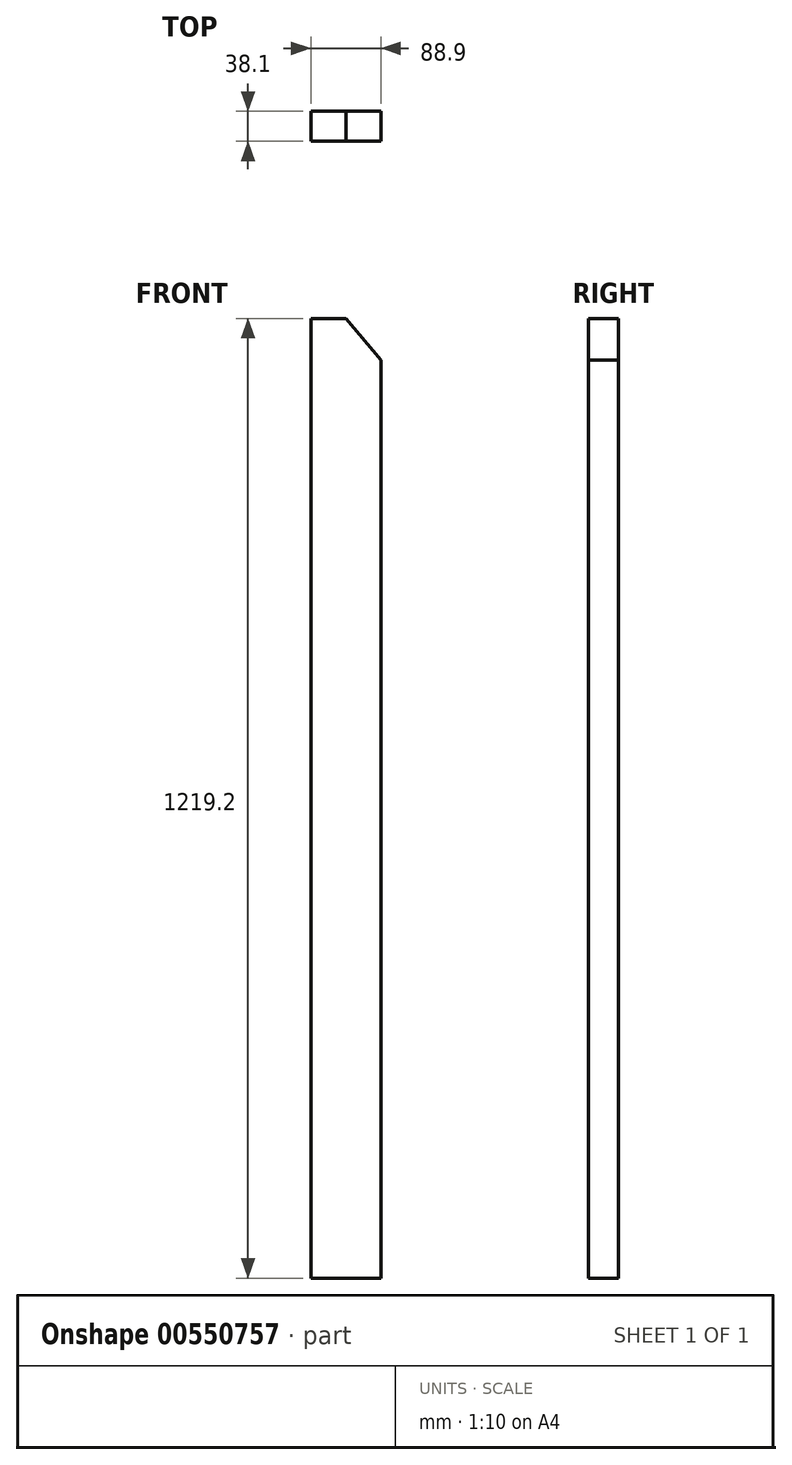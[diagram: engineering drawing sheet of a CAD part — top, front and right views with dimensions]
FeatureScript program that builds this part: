
annotation { "Feature Type Name" : "Feature", "Feature Type Description" : "" }
export const myFeature = defineFeature(function(context is Context, id is Id, definition is map)
    precondition{}
    {
        {
            var Q0;
            Q0=qCreatedBy(makeId("Front.planeOp"),FACE);
            var sketch = newSketch(context, id + "F0", { "sketchPlane" : qUnion([Q0])});
            skLineSegment(sketch, "E0", {"start": v(0, 0) * mm, "end": v(88.9, 0) * mm});
            skLineSegment(sketch, "E1", {"start": v(88.9, 0) * mm, "end": v(88.9, 1166.23) * mm});
            skLineSegment(sketch, "E2", {"start": v(88.9, 1166.23) * mm, "end": v(44.45, 1219.2) * mm});
            skLineSegment(sketch, "E3", {"start": v(0, 1219.2) * mm, "end": v(0, 0) * mm});
            skLineSegment(sketch, "E4", {"start": v(0, 1219.2) * mm, "end": v(44.45, 1219.2) * mm});
            skPoint(sketch, "E5.orphan", {"position": v(0, 1272.17) * mm});
            skSolve(sketch);
        }
        {
            var Q0;
            Q0=makeQuery(id+"F0.imprint","IMPRINT",FACE,{"disambiguationData":[TD([[makeQuery(id+"F0.imprint","IMPRINT",EDGE,{"derivedFrom":sQuery(id+"F0.wireOp",EDGE,"E0")}),1.0]])]});
            var Q1;
            Q1 = qConstructionFilter(qBodyType(qCreatedBy(id + "F0" ,EDGE), BodyType.WIRE), ConstructionObject.NO);
            extrude(context, id + "F1", {"entities" : qUnion([Q0]), "surfaceEntities" : qUnion([Q1]), "oppositeDirection" : true, "depth" : 38.1 * mm, "offsetDistance" : 25.4 * mm});
        }
    });
